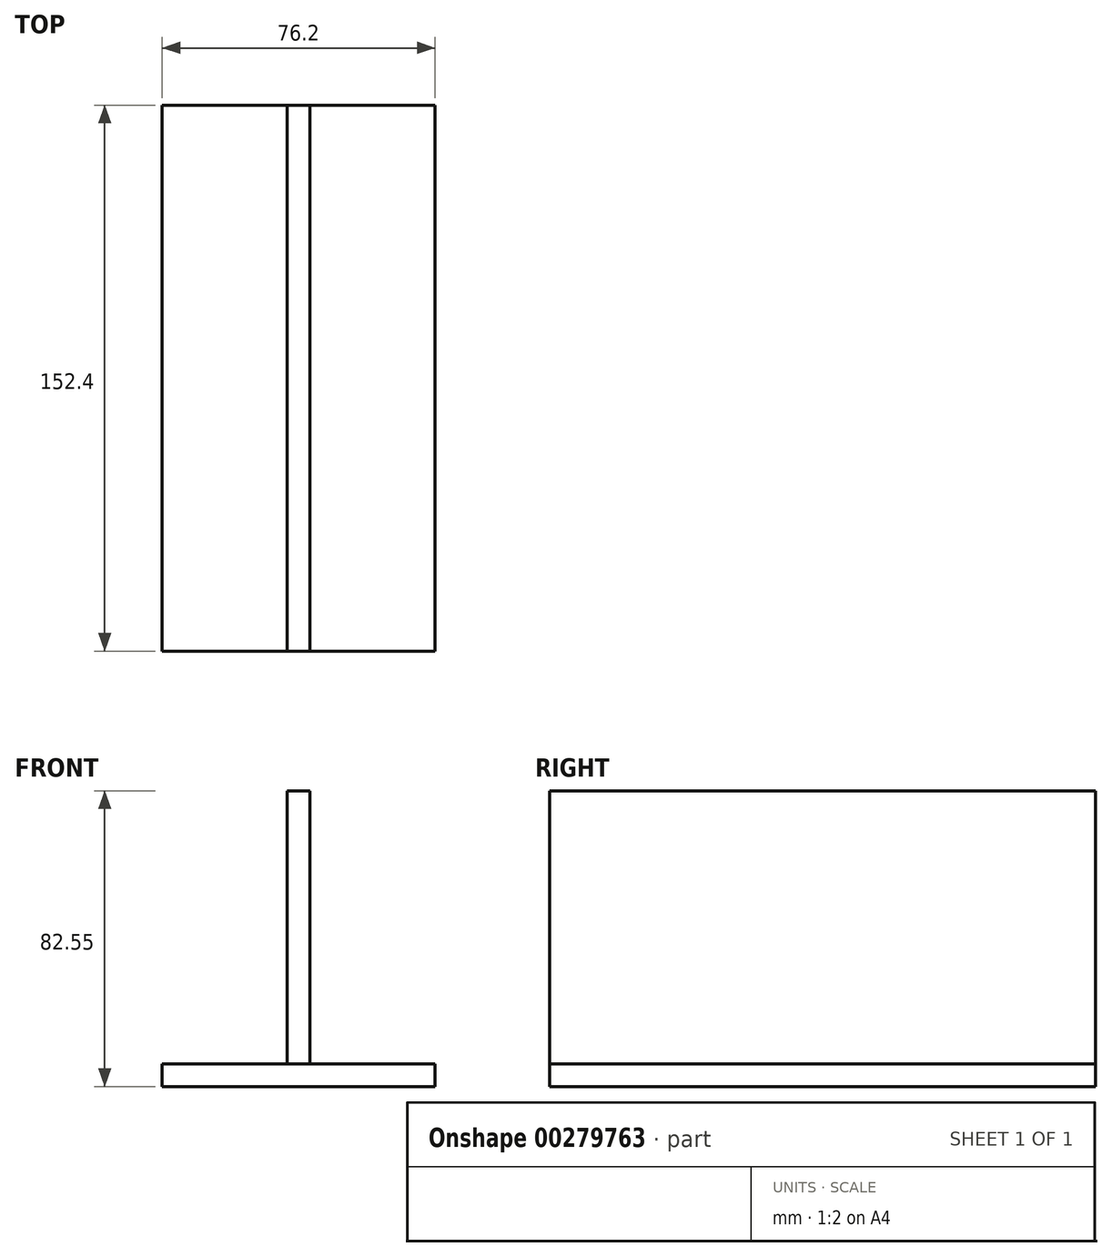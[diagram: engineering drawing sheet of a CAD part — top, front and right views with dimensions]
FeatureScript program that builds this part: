
annotation { "Feature Type Name" : "Feature", "Feature Type Description" : "" }
export const myFeature = defineFeature(function(context is Context, id is Id, definition is map)
    precondition{}
    {
        {
            var Q0;
            Q0=qCreatedBy(makeId("Front.planeOp"),FACE);
            var sketch = newSketch(context, id + "F0", { "sketchPlane" : qUnion([Q0])});
            skLineSegment(sketch, "E0.bottom", {"start": v(-38.1, 0) * mm, "end": v(38.1, 0) * mm});
            skLineSegment(sketch, "E0.top", {"start": v(-38.1, -6.35) * mm, "end": v(38.1, -6.35) * mm});
            skLineSegment(sketch, "E0.left", {"start": v(-38.1, 0) * mm, "end": v(-38.1, -6.35) * mm});
            skLineSegment(sketch, "E0.right", {"start": v(38.1, 0) * mm, "end": v(38.1, -6.35) * mm});
            skLineSegment(sketch, "E1.bottom", {"start": v(-3.18, 76.2) * mm, "end": v(3.17, 76.2) * mm});
            skLineSegment(sketch, "E1.top", {"start": v(-3.17, 0) * mm, "end": v(3.17, 0) * mm});
            skLineSegment(sketch, "E1.left", {"start": v(3.17, 76.2) * mm, "end": v(3.18, 0) * mm});
            skLineSegment(sketch, "E1.right", {"start": v(-3.17, 76.2) * mm, "end": v(-3.17, 0) * mm});
            skSolve(sketch);
        }
        {
            var Q0;
            Q0=makeQuery(id+"F0.imprint","IMPRINT",FACE,{"disambiguationData":[TD([[makeQuery(id+"F0.imprint","IMPRINT",EDGE,{"derivedFrom":sQuery(id+"F0.wireOp",EDGE,"E1.bottom")}),-1.0]])]});
            extrude(context, id + "F1", {"entities" : qUnion([Q0]), "depth" : 152.4 * mm});
        }
        {
            var Q0;
            Q0=makeQuery(id+"F0.imprint","IMPRINT",FACE,{"disambiguationData":[TD([[makeQuery(id+"F0.imprint","IMPRINT",EDGE,{"derivedFrom":sQuery(id+"F0.wireOp",EDGE,"E0.top")}),1.0]])]});
            extrude(context, id + "F2", {"entities" : qUnion([Q0]), "depth" : 152.4 * mm});
        }
    });
